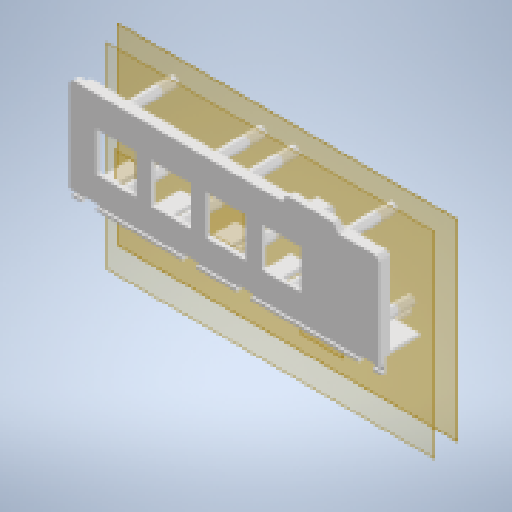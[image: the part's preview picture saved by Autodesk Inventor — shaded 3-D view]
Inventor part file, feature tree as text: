
AUTODESK INVENTOR PART (.ipt)
format: ipt  version: 2024.2 (Build 282272000, 272)  size: 843,264 bytes
history: native  units: in
note: dims shown in document units (in); Inventor stores cm internally (conversion verified against a paired STEP export)
features: reference x70, other x19, extrude x15, projected_geometry x6, sketch x5, fillet x4, plane x2, hole x1
ambient origin geometry x8: Origin, YZ Plane, XZ Plane, XY Plane, X Axis, Y Axis, Z Axis, Center Point
bodies: Solid1 (feature_tree)
feature tree (122):
  plane  "Work Plane1"
  other  "Bottom Case Offset"
  extrude  "Top Face"  Depth=0.1969in TaperAngle=0.0deg
  extrude  "Recept Cutouts"  Depth=0.1181in TaperAngle=0.0deg
  extrude  "Bosses"  Depth=1.0in TaperAngle=0.0deg
  other  "PCB Plane Offset"
  extrude  "PS Side Tall Barrier"  Depth=1.0in TaperAngle=0.0deg
  extrude  "PS Side Tall Barrier PCB"  Depth=0.1969in TaperAngle=0.0deg
  extrude  "Inner Lip"  Depth=0.2756in TaperAngle=0.0deg
  hole  "Boss Holes"  [1 undecoded]
  extrude  "Cord Relief"  Depth=0.125in TaperAngle=0.0deg
  fillet  "Boss Filets"  Radius=0.0197in
  other  "Relay Top"
  other  "PS Top"
  plane  "Work Plane7"
  extrude  "Barrier Relay"  Depth=0.125in
  extrude  "Barrier PSU"  Depth=0.125in TaperAngle=0.0deg
  fillet  "Outside corner fillets"  Radius=0.0079in
  fillet  "Outer Boss Fillets"  Radius=0.0079in
  other  "TopReceptSeatOffset"
  extrude  "Recept Inset"  Depth=0.125in
  extrude  "TopFace Interlock"  Depth=0.125in
  extrude  "Extrusion13"  Depth=0.125in
  extrude  "Extrusion14"  Depth=0.125in TaperAngle=0.0deg
  extrude  "Extrusion15"  Depth=0.125in TaperAngle=0.0deg
  extrude  "Extrusion16"  Depth=0.125in
  fillet  "Fillet5"  Radius=0.0591in
  sketch  "Sketch1"  dims[d0=0.1969in d1=0.0in d3=0.1181in d4=0.0in]
  reference  "Reference3"
  reference  "Reference4"
  reference  "Reference6"
  reference  "Reference7"
  reference  "Reference9"
  reference  "Reference10"
  reference  "Reference11"
  reference  "Reference13"
  reference  "Reference15"
  reference  "Reference17"
  reference  "Reference18"
  reference  "Reference21"
  reference  "Reference23"
  reference  "Reference29"
  sketch  "Sketch6"  dims[d5=0.0079in d6=0.1181in d7=0.0in]
  projected_geometry  "Projected Loop1"
  projected_geometry  "Projected Loop2"
  projected_geometry  "Projected Loop3"
  reference  "Reference43"
  reference  "Reference44"
  reference  "Reference45"
  reference  "Reference46"
  reference  "Reference50"
  reference  "Reference51"
  reference  "Reference52"
  reference  "Reference53"
  reference  "Reference54"
  reference  "Reference55"
  reference  "Reference56"
  reference  "Reference57"
  reference  "Reference58"
  reference  "Reference59"
  reference  "Reference60"
  sketch  "Sketch14"  dims[d8=0.0197in d11=1.0in d12=0.0in]
  reference  "Reference61"
  reference  "Reference62"
  reference  "Reference64"
  reference  "Reference65"
  reference  "Reference66"
  reference  "Reference67"
  projected_geometry  "Projected Loop4"
  reference  "Reference69"
  reference  "Reference70"
  reference  "Reference71"
  reference  "Reference72"
  reference  "Reference73"
  reference  "Reference74"
  reference  "Reference75"
  reference  "Reference76"
  reference  "Reference77"
  reference  "Reference78"
  reference  "Reference79"
  reference  "Reference80"
  reference  "Reference81"
  reference  "Reference82"
  reference  "Reference83"
  reference  "Reference84"
  reference  "Reference85"
  reference  "Reference86"
  reference  "Reference87"
  reference  "Reference88"
  reference  "Reference89"
  reference  "Reference90"
  reference  "Reference91"
  reference  "Reference92"
  reference  "Reference93"
  reference  "Reference95"
  reference  "Reference96"
  reference  "Reference97"
  reference  "Reference98"
  reference  "Reference99"
  projected_geometry  "Projected Loop5"
  sketch  "Sketch17"  dims[d13=0.0079in d14=1.0in d15=0.0in]
  reference  "Reference100"
  reference  "Reference101"
  reference  "Reference102"
  reference  "Reference103"
  reference  "Reference104"
  sketch  "Sketch18"  dims[d16=0.0079in d23=0.1969in d24=0.0in d26=0.0849in d27=0.224in d28=0.375in d29=0.25in d30=0.5635in d31=0.5in d32=0.8108in d34=0.2756in d35=0.0in d38=0.125in d53=1.0in d54=0.0in d55=0.0197in d56=0.0197in d57=1.0in d58=0.0in d59=0.0079in d60=0.0079in d62=0.0787in d63=0.125in d64=0.125in d67=0.1575in d68=0.0in d69=0.079in d70=0.0in d73=0.0787in d74=0.0591in d75=0.0394in d77=0.0394in d78=0.0394in d80=1.0in d81=0.0in d83=0.0in d84=0.0in d85=1.0in d86=0.0in d96=0.0394in d97=0.0394in d98=0.0394in d99=0.0394in d100=0.0394in d101=0.0118in d102=0.0118in d103=0.0118in d104=0.0118in d105=0.0118in d106=0.0118in d107=0.0118in d108=0.0118in d109=0.0039in d110=0.0787in d111=0.1437in d112=0.1in d113=0.0787in d114=0.0118in d115=0.0118in d116=1.0in d117=0.0in d118=1.0in d119=0.0in d120=0.125in]
  projected_geometry  "Projected Loop6"
  other  "<userpath>\Dropbox\elec\Mechanical\ReefVoltEssential\_TOP.iam"
  other  "_TOP.iam"
  other  "reefvolt_power_essentials_ESP32:2"
  other  "J200_PLA"
  other  "J200_PLD"
  other  "J200_PLC"
  other  "J200_PLB"
  other  "reefvolt_power_essentials_ESP32_BOARD:1"
  other  "RV_ES_Bottom:1"
  other  "U101"
  other  "RL200_PLB"
  other  "RL200_PLC"
  other  "RL200_PLD"
  other  "RL200_PLA"
note: 1 required parameter value undecoded (feature->parameter linkage not recoverable at this tier; creation-order binding heuristic only, values carry confidence <= 0.55)
